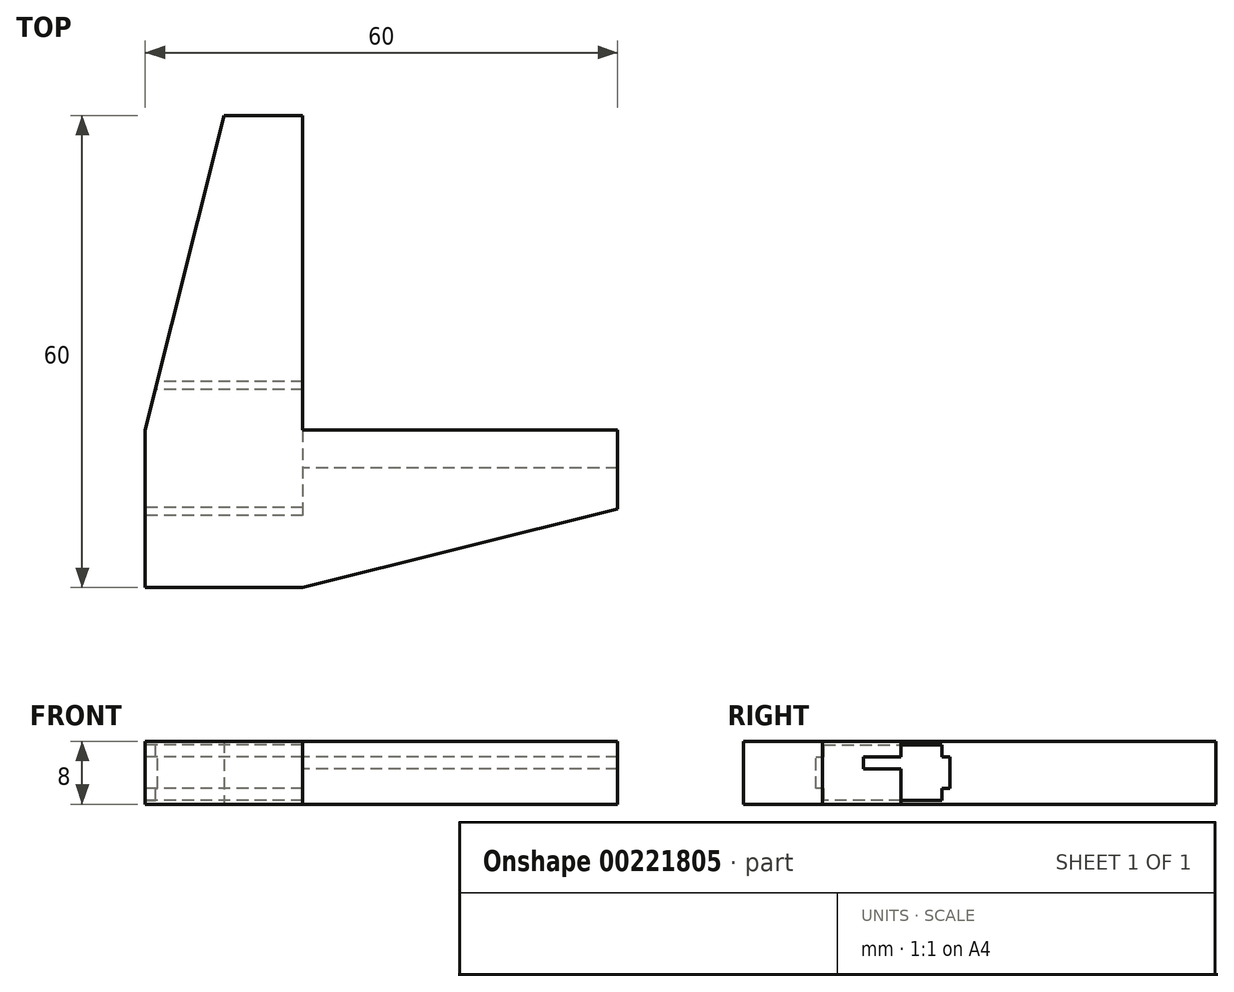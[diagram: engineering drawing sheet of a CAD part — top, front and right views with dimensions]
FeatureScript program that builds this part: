
annotation { "Feature Type Name" : "Feature", "Feature Type Description" : "" }
export const myFeature = defineFeature(function(context is Context, id is Id, definition is map)
    precondition{}
    {
        {
            var Q0;
            Q0=qCreatedBy(makeId("Top.planeOp"),FACE);
            var sketch = newSketch(context, id + "F0", { "sketchPlane" : qUnion([Q0])});
            skLineSegment(sketch, "E0", {"start": v(0, 0) * mm, "end": v(0, 40) * mm});
            skLineSegment(sketch, "E1", {"start": v(0, 0) * mm, "end": v(40, 0) * mm});
            skLineSegment(sketch, "E2", {"start": v(40, 0) * mm, "end": v(40, -10) * mm});
            skLineSegment(sketch, "E3", {"start": v(40, -10) * mm, "end": v(0, -20) * mm});
            skLineSegment(sketch, "E4", {"start": v(0, -20) * mm, "end": v(-20, -20) * mm});
            skLineSegment(sketch, "E5", {"start": v(-20, -20) * mm, "end": v(-20, 0) * mm});
            skLineSegment(sketch, "E6", {"start": v(-20, 0) * mm, "end": v(-10, 40) * mm});
            skLineSegment(sketch, "E7", {"start": v(-10, 40) * mm, "end": v(0, 40) * mm});
            skSolve(sketch);
        }
        {
            var Q0;
            Q0=makeQuery(id+"F0.imprint","IMPRINT",FACE,{"disambiguationData":[TD([[makeQuery(id+"F0.imprint","IMPRINT",EDGE,{"derivedFrom":sQuery(id+"F0.wireOp",EDGE,"E0")}),1.0]])]});
            extrude(context, id + "F1", {"entities" : qUnion([Q0]), "endBound" : BoundingType.SYMMETRIC, "depth" : 8 * mm});
        }
        {
            var Q0;
            Q0=makeQuery(id+"F1.opExtrude","SWEPT_FACE",FACE,{"disambiguationData":[OSD([sQuery(id+"F0.wireOp",EDGE,"E5")])]});
            var sketch = newSketch(context, id + "F2", { "sketchPlane" : qUnion([Q0])});
            skLineSegment(sketch, "E8", {"start": v(-6.2, 2) * mm, "end": v(-5.2, 2) * mm});
            skLineSegment(sketch, "E9", {"start": v(-5.2, 2) * mm, "end": v(-5.2, 3.5) * mm});
            skLineSegment(sketch, "E10", {"start": v(-5.2, 3.5) * mm, "end": v(9.8, 3.5) * mm});
            skLineSegment(sketch, "E11", {"start": v(9.8, 3.5) * mm, "end": v(9.8, 2) * mm});
            skLineSegment(sketch, "E12", {"start": v(9.8, 2) * mm, "end": v(10.8, 2) * mm});
            skLineSegment(sketch, "E13", {"start": v(10.8, 2) * mm, "end": v(10.8, -2) * mm});
            skLineSegment(sketch, "E14", {"start": v(10.8, -2) * mm, "end": v(9.8, -2) * mm});
            skLineSegment(sketch, "E15", {"start": v(9.8, -2) * mm, "end": v(9.8, -3.5) * mm});
            skLineSegment(sketch, "E16", {"start": v(9.8, -3.5) * mm, "end": v(-5.2, -3.5) * mm});
            skLineSegment(sketch, "E17", {"start": v(-5.2, -3.5) * mm, "end": v(-5.2, -2) * mm});
            skLineSegment(sketch, "E18", {"start": v(-5.2, -2) * mm, "end": v(-6.2, -2) * mm});
            skLineSegment(sketch, "E19", {"start": v(-6.2, -2) * mm, "end": v(-6.2, 2) * mm});
            skLineSegment(sketch, "E20", {"start": v(2.3, 3.5) * mm, "end": v(2.3, -3.5) * mm, "construction": true});
            skLineSegment(sketch, "E21", {"start": v(-6.2, 0) * mm, "end": v(10.8, 0) * mm, "construction": true});
            skLineSegment(sketch, "E22.bottom", {"start": v(-0.2, 2) * mm, "end": v(4.8, 2) * mm});
            skLineSegment(sketch, "E22.top", {"start": v(-0.2, 0.5) * mm, "end": v(4.8, 0.5) * mm});
            skLineSegment(sketch, "E22.left", {"start": v(-0.2, 2) * mm, "end": v(-0.2, 0.5) * mm});
            skLineSegment(sketch, "E22.right", {"start": v(4.8, 2) * mm, "end": v(4.8, 0.5) * mm});
            skLineSegment(sketch, "E23", {"start": v(2.3, 2) * mm, "end": v(2.3, 0.5) * mm, "construction": true});
            skLineSegment(sketch, "E24", {"start": v(-0.2, 1.25) * mm, "end": v(4.8, 1.25) * mm, "construction": true});
            skPoint(sketch, "E25", {"position": v(2.3, 2) * mm});
            skLineSegment(sketch, "E26.0", {"start": v(-0.1, 1.9) * mm, "end": v(4.7, 1.9) * mm});
            skLineSegment(sketch, "E26.1", {"start": v(-0.1, 1.9) * mm, "end": v(-0.1, 0.6) * mm});
            skLineSegment(sketch, "E26.2", {"start": v(-0.1, 0.6) * mm, "end": v(4.7, 0.6) * mm});
            skLineSegment(sketch, "E26.3", {"start": v(4.7, 1.9) * mm, "end": v(4.7, 0.6) * mm});
            skPoint(sketch, "E27", {"position": v(0, 0) * mm});
            skSolve(sketch);
        }
        {
            var Q0;
            Q0=qSketchRegion(id+"F2",true);
            var Q1;
            {var subQ0=sQuery(id+"F2.wireOp",EDGE,"E26.1");Q1=makeQuery(id+"F2.imprint","IMPRINT",FACE,{"disambiguationData":[TD([[makeQuery(id+"F2.imprint","IMPRINT",EDGE,{"derivedFrom":subQ0}),1.0]])]});}
            var Q2;
            {var subQ0=sQuery(id+"F2.wireOp",EDGE,"E26.3");Q2=makeQuery(id+"F2.imprint","IMPRINT",FACE,{"disambiguationData":[TD([[makeQuery(id+"F2.imprint","IMPRINT",EDGE,{"derivedFrom":subQ0}),-1.0]])]});}
            var Q3;
            {var subQ4=sQuery(id+"F2.wireOp",EDGE,"E22.right");Q3=makeQuery(id+"F2.imprint","IMPRINT",FACE,{"disambiguationData":[TD([[makeQuery(id+"F2.imprint","IMPRINT",EDGE,{"derivedFrom":subQ4}),-1.0]])]});}
            var Q4;
            {var subQ0=sQuery(id+"F2.wireOp",EDGE,"E22.left");Q4=makeQuery(id+"F2.imprint","IMPRINT",FACE,{"disambiguationData":[TD([[makeQuery(id+"F2.imprint","IMPRINT",EDGE,{"derivedFrom":subQ0}),1.0]])]});}
            var Q5;
            Q5=makeQuery(id+"F1.opExtrude","SWEPT_FACE",FACE,{"disambiguationData":[OSD([sQuery(id+"F0.wireOp",EDGE,"E0")])]});
            extrude(context, id + "F3", {"entities" : qUnion([Q0, Q1, Q2, Q3, Q4]), "operationType" : NewBodyOperationType.REMOVE, "endBound" : BoundingType.UP_TO_SURFACE, "oppositeDirection" : true, "endBoundEntityFace" : qUnion([Q5]), "depth" : 25 * mm});
        }
        {
            var Q0;
            {var subQ4=sQuery(id+"F2.wireOp",EDGE,"E22.right");Q0=makeQuery(id+"F2.imprint","IMPRINT",FACE,{"disambiguationData":[TD([[makeQuery(id+"F2.imprint","IMPRINT",EDGE,{"derivedFrom":subQ4}),-1.0]])]});}
            var Q1;
            {var subQ0=sQuery(id+"F2.wireOp",EDGE,"E26.3");Q1=makeQuery(id+"F2.imprint","IMPRINT",FACE,{"disambiguationData":[TD([[makeQuery(id+"F2.imprint","IMPRINT",EDGE,{"derivedFrom":subQ0}),-1.0]])]});}
            var Q2;
            {var subQ0=sQuery(id+"F2.wireOp",EDGE,"E26.1");Q2=makeQuery(id+"F2.imprint","IMPRINT",FACE,{"disambiguationData":[TD([[makeQuery(id+"F2.imprint","IMPRINT",EDGE,{"derivedFrom":subQ0}),1.0]])]});}
            var Q3;
            {var subQ0=sQuery(id+"F2.wireOp",EDGE,"E22.left");Q3=makeQuery(id+"F2.imprint","IMPRINT",FACE,{"disambiguationData":[TD([[makeQuery(id+"F2.imprint","IMPRINT",EDGE,{"derivedFrom":subQ0}),1.0]])]});}
            var Q4;
            Q4=makeQuery(id+"F1.opExtrude","SWEPT_FACE",FACE,{"disambiguationData":[OSD([sQuery(id+"F0.wireOp",EDGE,"E2")])]});
            extrude(context, id + "F4", {"entities" : qUnion([Q0, Q1, Q2, Q3]), "operationType" : NewBodyOperationType.REMOVE, "endBound" : BoundingType.UP_TO_SURFACE, "oppositeDirection" : true, "endBoundEntityFace" : qUnion([Q4]), "depth" : 25 * mm});
        }
    });
